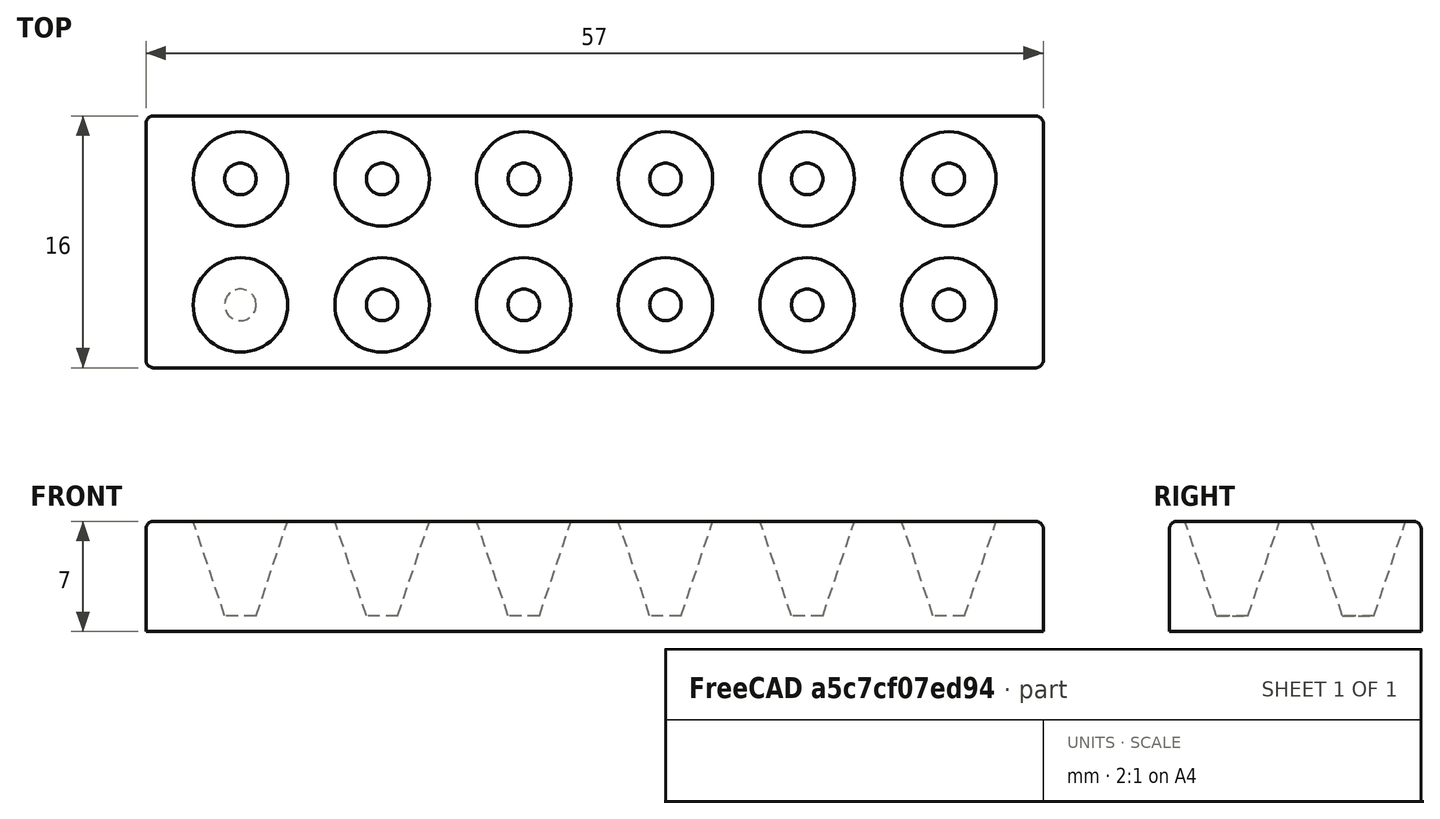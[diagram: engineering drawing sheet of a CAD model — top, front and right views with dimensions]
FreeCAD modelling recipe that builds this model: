
FCSTD DOCUMENT  (FreeCAD 0.21R33694 (Git))
Label: npatris_repte2
License: All rights reserved
LicenseURL: https://en.wikipedia.org/wiki/All_rights_reserved
objects: Part::Box×1, Part::Cone×1, Part::FeaturePython×1, Part::Fillet×1, Part::Cut×1
note: 4 computed .brp shape members not serialized (recipe doc carries the construction recipe); baked Part::Feature solids carry a one-line shape summary decoded from their .brp

FEATURE [Part::Box] Box  label="Base"
  AttacherType = Attacher::AttachEngine3D
  Height = 7
  Length = 57
  Width = 16
FEATURE [Part::Cone] Cone  label="Con"
  Angle = 360
  AttacherType = Attacher::AttachEngine3D
  Height = 6
  Placement = pos=(6,4,1) rot=(0,0,1;0rad)
  Radius1 = 1
  Radius2 = 3
FEATURE [Part::FeaturePython] Array  # Draft array (typed FeaturePython)
  AlwaysSyncPlacement = false
  Angle = 360
  ArrayType = 0
  Axis = (0,0,1)
  Base = -> Cone
  Center = (0,0,0)
  Count = 12
  ExpandArray = false
  Fuse = false
  IntervalAxis = (0,0,0)
  IntervalX = (9,0,0)
  IntervalY = (0,8,0)
  IntervalZ = (0,0,100)
  NumberCircles = 3
  NumberPolar = 5
  NumberX = 6
  NumberY = 2
  NumberZ = 1
  PlacementList = 12 placements: [(6,4,1),(6,12,1),(15,4,1),(15,12,1),(24,4,1),(24,12,1),(33,4,1),(33,12,1),(42,4,1),(42,12,1),(51,4,1),(51,12,1)]
  RadialDistance = 50
  ScaleList = (12) [(1,1,1),(1,1,1),(1,1,1),(1,1,1),(1,1,1),(1,1,1),(1,1,1),(1,1,1),(1,1,1),(1,1,1),(1,1,1),(1,1,1)]
  Symmetry = 1
  TangentialDistance = 25
FEATURE [Part::Fillet] Fillet
  Base = -> Box
  Edges = 8 edges r=0.5: [Edge1,Edge2,Edge3,Edge5,Edge6,Edge7,Edge10,Edge12]
FEATURE [Part::Cut] Cut  label="Ouera"
  Base = -> Fillet
  Tool = -> Array
